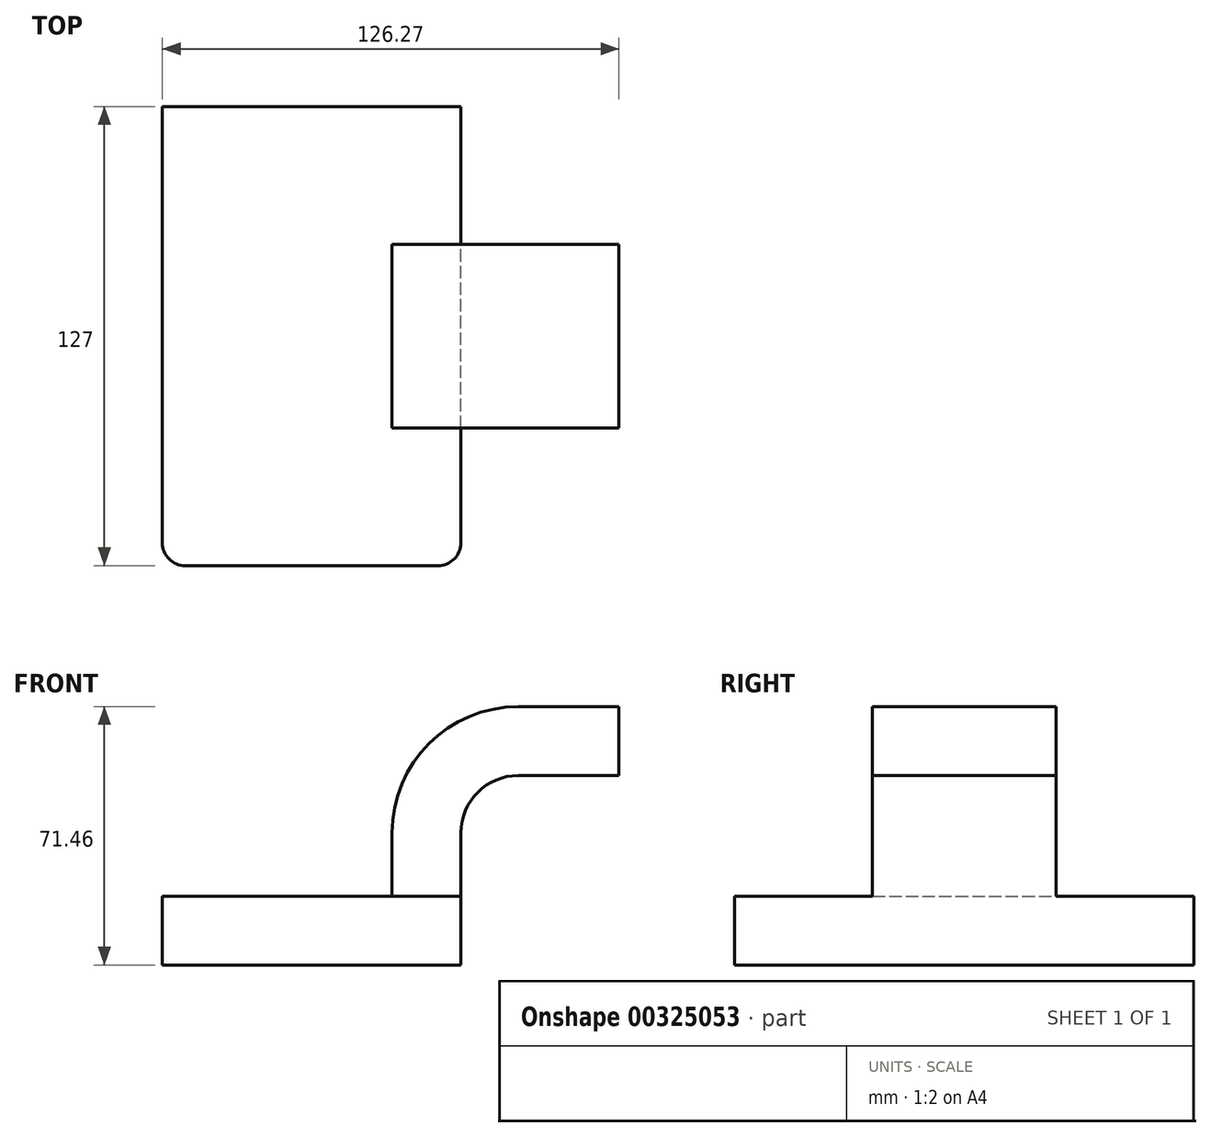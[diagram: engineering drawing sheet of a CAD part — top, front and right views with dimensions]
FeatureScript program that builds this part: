
annotation { "Feature Type Name" : "Feature", "Feature Type Description" : "" }
export const myFeature = defineFeature(function(context is Context, id is Id, definition is map)
    precondition{}
    {
        {
            var Q0;
            Q0=qCreatedBy(makeId("Front.planeOp"),FACE);
            var sketch = newSketch(context, id + "F0", { "sketchPlane" : qUnion([Q0])});
            skLineSegment(sketch, "E0.bottom", {"start": v(-41.28, -9.53) * mm, "end": v(41.28, -9.53) * mm});
            skLineSegment(sketch, "E0.top", {"start": v(-41.28, 9.52) * mm, "end": v(41.28, 9.52) * mm});
            skLineSegment(sketch, "E0.left", {"start": v(-41.28, -9.53) * mm, "end": v(-41.28, 9.52) * mm});
            skLineSegment(sketch, "E0.right", {"start": v(41.27, -9.53) * mm, "end": v(41.27, 9.52) * mm});
            skPoint(sketch, "E0.middle", {"position": v(0, 0) * mm});
            skLineSegment(sketch, "E1.bottom", {"start": v(60.32, 38.1) * mm, "end": v(111.12, 38.1) * mm});
            skLineSegment(sketch, "E1.top", {"start": v(60.32, 66.67) * mm, "end": v(111.12, 66.67) * mm});
            skLineSegment(sketch, "E1.left", {"start": v(60.32, 38.1) * mm, "end": v(60.32, 66.67) * mm});
            skLineSegment(sketch, "E1.right", {"start": v(111.12, 38.1) * mm, "end": v(111.12, 66.67) * mm});
            skPoint(sketch, "E1.middle", {"position": v(85.72, 52.39) * mm});
            skLineSegment(sketch, "E2", {"start": v(41.28, 9.52) * mm, "end": v(41.28, 27) * mm});
            skArc(sketch, "E3", {"start": v(41.27, 27) * mm, "mid": v(45.92, 38.23) * mm, "end": v(57.15, 42.88) * mm});
            skLineSegment(sketch, "E4", {"start": v(57.15, 42.88) * mm, "end": v(84.99, 42.88) * mm});
            skLineSegment(sketch, "E5.0", {"start": v(57.15, 61.93) * mm, "end": v(84.99, 61.93) * mm});
            skArc(sketch, "E5.1", {"start": v(22.22, 27) * mm, "mid": v(32.45, 51.7) * mm, "end": v(57.15, 61.93) * mm});
            skLineSegment(sketch, "E5.2", {"start": v(22.23, 9.52) * mm, "end": v(22.23, 27) * mm});
            skFitSpline(sketch, "E6", {"points": [v(-41.28, 9.52) * mm, v(57.15, 61.93) * mm], "startDerivative": vector(0, 63.1) * mm, "endDerivative": vector(148.51, 0) * mm});
            skLineSegment(sketch, "E7", {"start": v(84.99, 61.93) * mm, "end": v(84.99, 42.88) * mm});
            skSolve(sketch);
        }
        {
            var Q0;
            Q0=makeQuery(id+"F0.imprint","IMPRINT",FACE,{"disambiguationData":[TD([[makeQuery(id+"F0.imprint","IMPRINT",EDGE,{"derivedFrom":sQuery(id+"F0.wireOp",EDGE,"E0.bottom")}),1.0]])]});
            extrude(context, id + "F1", {"entities" : qUnion([Q0]), "endBound" : BoundingType.SYMMETRIC, "depth" : 127 * mm});
        }
        {
            var Q0;
            {var subQ0=sQuery(id+"F0.wireOp",EDGE,"E2");Q0=makeQuery(id+"F0.imprint","IMPRINT",FACE,{"disambiguationData":[TD([[makeQuery(id+"F0.imprint","IMPRINT",EDGE,{"derivedFrom":subQ0}),1.0]])]});}
            var Q1;
            {var subQ5=sQuery(id+"F0.wireOp",EDGE,"E7");Q1=makeQuery(id+"F0.imprint","IMPRINT",FACE,{"disambiguationData":[TD([[makeQuery(id+"F0.imprint","IMPRINT",EDGE,{"derivedFrom":subQ5}),-1.0]])]});}
            extrude(context, id + "F2", {"entities" : qUnion([Q0, Q1]), "operationType" : NewBodyOperationType.ADD, "endBound" : BoundingType.SYMMETRIC, "depth" : 50.8 * mm});
        }
        {
            var Q0;
            Q0=makeQuery(id+"F0.imprint","IMPRINT",FACE,{"disambiguationData":[TD([[makeQuery(id+"F0.imprint","IMPRINT",EDGE,{"derivedFrom":sQuery(id+"F0.wireOp",EDGE,"E5.1")}),1.0]])]});
            extrude(context, id + "F3", {"entities" : qUnion([Q0]), "operationType" : NewBodyOperationType.ADD, "endBound" : BoundingType.SYMMETRIC, "depth" : 15.88 * mm});
        }
        {
            var Q0;
            Q0=makeQuery(id+"F1.opExtrude","CAP_EDGE",EDGE,{"disambiguationData":[OSD([sQuery(id+"F0.wireOp",EDGE,"E0.left")])],"isStart":false});
            var Q1;
            Q1=makeQuery(id+"F1.opExtrude","CAP_EDGE",EDGE,{"disambiguationData":[OSD([sQuery(id+"F0.wireOp",EDGE,"E0.right")])],"isStart":false});
            fillet(context, id + "F4", {"entities" : qUnion([Q0, Q1]), "radius" : 6.35 * mm, "tangentPropagation" : true, "allowEdgeOverflow" : false});
        }
    });
